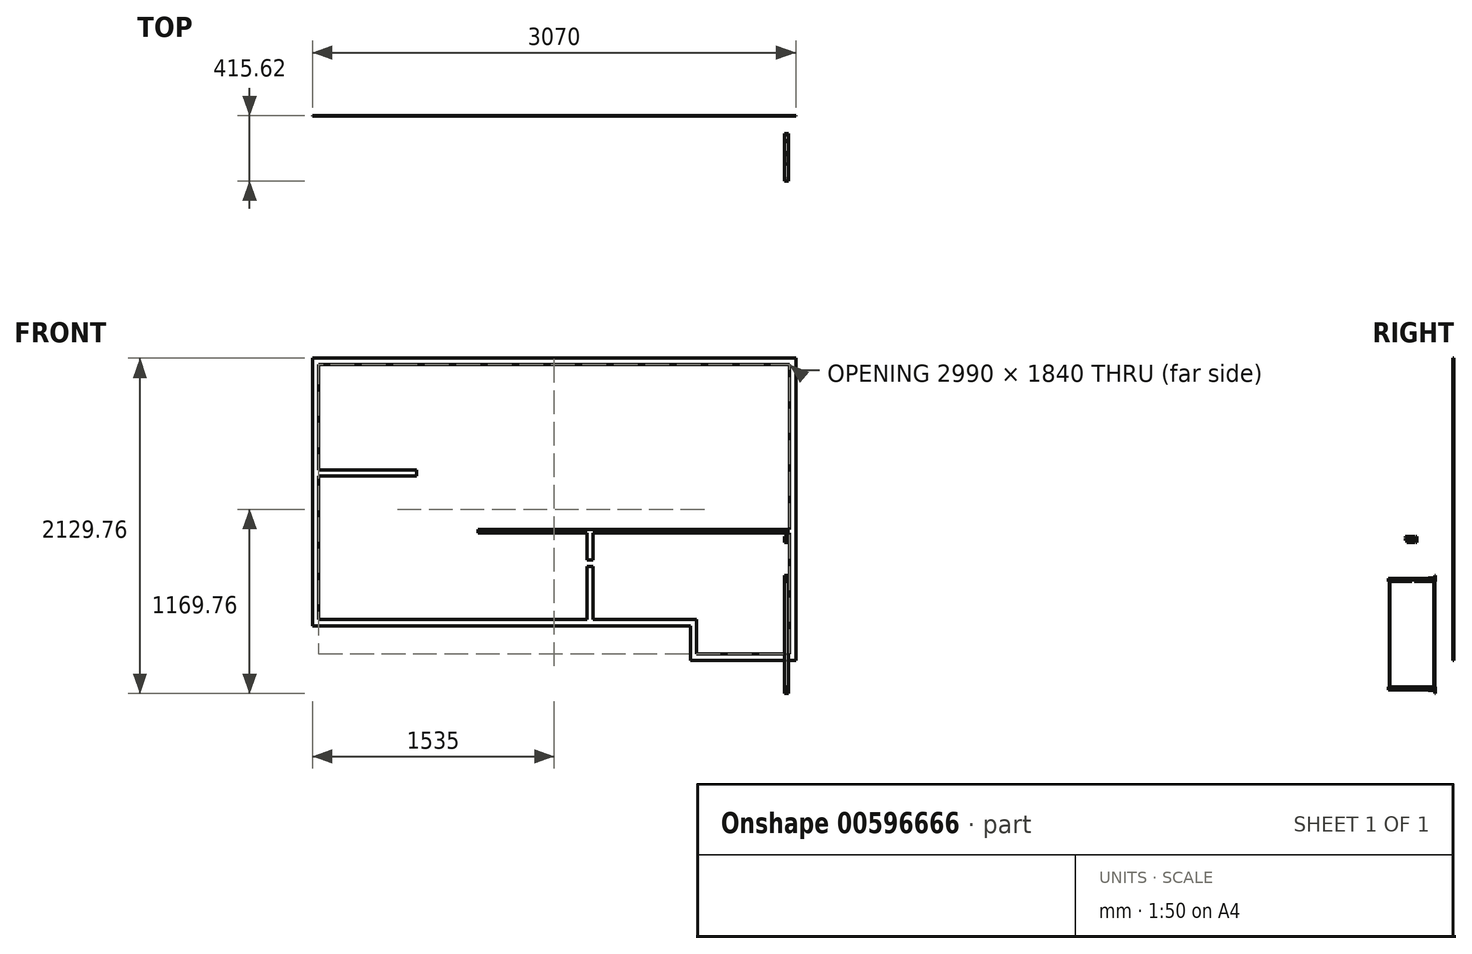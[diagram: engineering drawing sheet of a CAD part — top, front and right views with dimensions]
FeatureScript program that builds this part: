
annotation { "Feature Type Name" : "Feature", "Feature Type Description" : "" }
export const myFeature = defineFeature(function(context is Context, id is Id, definition is map)
    precondition{}
    {
        {
            var Q0;
            Q0=qCreatedBy(makeId("Front.planeOp"),FACE);
            var sketch = newSketch(context, id + "F0", { "sketchPlane" : qUnion([Q0])});
            skLineSegment(sketch, "E0.bottom", {"start": v(-2999.25, 2139.45) * mm, "end": v(70.75, 2139.45) * mm});
            skLineSegment(sketch, "E0.top", {"start": v(-599.25, 219.45) * mm, "end": v(70.75, 219.45) * mm});
            skLineSegment(sketch, "E0.left", {"start": v(-2999.25, 2139.45) * mm, "end": v(-2999.25, 439.45) * mm});
            skLineSegment(sketch, "E0.right", {"start": v(70.75, 2139.45) * mm, "end": v(70.75, 219.45) * mm});
            skLineSegment(sketch, "E1", {"start": v(-2999.25, 439.45) * mm, "end": v(-599.25, 439.45) * mm});
            skLineSegment(sketch, "E2", {"start": v(-599.25, 439.45) * mm, "end": v(-599.25, 219.45) * mm});
            skLineSegment(sketch, "E3.0", {"start": v(-2959.25, 2099.45) * mm, "end": v(-2959.25, 479.45) * mm});
            skLineSegment(sketch, "E3.1", {"start": v(30.75, 2099.45) * mm, "end": v(30.75, 1079.45) * mm});
            skLineSegment(sketch, "E3.2", {"start": v(-559.25, 259.45) * mm, "end": v(30.75, 259.45) * mm});
            skLineSegment(sketch, "E3.3", {"start": v(-2959.25, 2099.45) * mm, "end": v(30.75, 2099.45) * mm});
            skLineSegment(sketch, "E3.4", {"start": v(-559.25, 479.45) * mm, "end": v(-559.25, 259.45) * mm});
            skLineSegment(sketch, "E3.5", {"start": v(-2959.25, 479.45) * mm, "end": v(-559.25, 479.45) * mm});
            skLineSegment(sketch, "E4.top", {"start": v(-2959.25, 1029.45) * mm, "end": v(-1989.25, 1029.45) * mm});
            skLineSegment(sketch, "E4.left", {"start": v(-2959.25, 1069.45) * mm, "end": v(-2959.25, 1029.45) * mm});
            skLineSegment(sketch, "E4.right", {"start": v(30.75, 1079.45) * mm, "end": v(30.75, 1029.45) * mm});
            skLineSegment(sketch, "E5.bottom", {"start": v(-2339.25, 2099.45) * mm, "end": v(-2299.25, 2099.45) * mm});
            skLineSegment(sketch, "E5.top", {"start": v(-2339.25, 1069.45) * mm, "end": v(-2299.25, 1069.45) * mm});
            skLineSegment(sketch, "E5.left", {"start": v(-2339.25, 2099.45) * mm, "end": v(-2339.25, 1429.45) * mm});
            skLineSegment(sketch, "E5.right", {"start": v(-2299.25, 2099.45) * mm, "end": v(-2299.25, 1429.45) * mm});
            skLineSegment(sketch, "E6.bottom", {"start": v(-1989.25, 2099.45) * mm, "end": v(-1949.25, 2099.45) * mm});
            skLineSegment(sketch, "E6.left", {"start": v(-1989.25, 2099.45) * mm, "end": v(-1989.25, 1069.45) * mm});
            skLineSegment(sketch, "E6.right", {"start": v(-1949.25, 2099.45) * mm, "end": v(-1949.25, 1079.45) * mm});
            skLineSegment(sketch, "E7.bottom", {"start": v(-2959.25, 1429.45) * mm, "end": v(-2339.25, 1429.45) * mm});
            skLineSegment(sketch, "E7.top", {"start": v(-2959.25, 1389.45) * mm, "end": v(-2339.25, 1389.45) * mm});
            skLineSegment(sketch, "E7.left", {"start": v(-2959.25, 1429.45) * mm, "end": v(-2959.25, 1389.45) * mm});
            skLineSegment(sketch, "E7.right", {"start": v(-1989.25, 1429.45) * mm, "end": v(-1989.25, 1389.45) * mm});
            skLineSegment(sketch, "E8.bottom", {"start": v(-2649.25, 1029.45) * mm, "end": v(-2609.25, 1029.45) * mm});
            skLineSegment(sketch, "E8.top", {"start": v(-2649.25, 479.45) * mm, "end": v(-2609.25, 479.45) * mm});
            skLineSegment(sketch, "E8.left", {"start": v(-2649.25, 1029.45) * mm, "end": v(-2649.25, 479.45) * mm});
            skLineSegment(sketch, "E8.right", {"start": v(-2609.25, 1029.45) * mm, "end": v(-2609.25, 479.45) * mm});
            skLineSegment(sketch, "E9.bottom", {"start": v(-2609.25, 816.45) * mm, "end": v(-1256.25, 816.45) * mm});
            skLineSegment(sketch, "E9.top", {"start": v(-2609.25, 856.45) * mm, "end": v(-1949.25, 856.45) * mm});
            skLineSegment(sketch, "E9.left", {"start": v(-2609.25, 816.45) * mm, "end": v(-2609.25, 856.45) * mm});
            skLineSegment(sketch, "E9.right", {"start": v(30.75, 816.45) * mm, "end": v(30.75, 856.45) * mm});
            skLineSegment(sketch, "E10.bottom", {"start": v(-559.25, 479.45) * mm, "end": v(-599.25, 479.45) * mm});
            skLineSegment(sketch, "E10.top", {"start": v(-559.25, 816.45) * mm, "end": v(-599.25, 816.45) * mm});
            skLineSegment(sketch, "E10.left", {"start": v(-559.25, 479.45) * mm, "end": v(-559.25, 816.45) * mm});
            skLineSegment(sketch, "E10.right", {"start": v(-599.25, 479.45) * mm, "end": v(-599.25, 816.45) * mm});
            skLineSegment(sketch, "E11.top", {"start": v(-1989.25, 479.45) * mm, "end": v(-1949.25, 479.45) * mm});
            skLineSegment(sketch, "E11.left", {"start": v(-1989.25, 1069.45) * mm, "end": v(-1989.25, 856.45) * mm});
            skLineSegment(sketch, "E11.right", {"start": v(-1949.25, 1079.45) * mm, "end": v(-1949.25, 1079.45) * mm});
            skLineSegment(sketch, "E12", {"start": v(-1256.25, 479.45) * mm, "end": v(-1256.25, 816.45) * mm});
            skLineSegment(sketch, "E13", {"start": v(-1216.25, 1029.45) * mm, "end": v(-1216.25, 856.45) * mm});
            skLineSegment(sketch, "E14", {"start": v(-1949.25, 1049.45) * mm, "end": v(30.75, 1049.45) * mm});
            skPoint(sketch, "E14.endSnap0", {"position": v(30.75, 1054.45) * mm});
            skLineSegment(sketch, "E15", {"start": v(-1949.25, 1079.45) * mm, "end": v(-1949.25, 856.45) * mm});
            skLineSegment(sketch, "E16", {"start": v(30.75, 1079.45) * mm, "end": v(30.75, 259.45) * mm});
            skLineSegment(sketch, "E17", {"start": v(-1989.25, 1069.45) * mm, "end": v(-2959.25, 1069.45) * mm});
            skLineSegment(sketch, "E18", {"start": v(-1949.25, 1029.45) * mm, "end": v(30.75, 1029.45) * mm});
            skLineSegment(sketch, "E19", {"start": v(-2959.25, 479.45) * mm, "end": v(-2999.25, 439.45) * mm});
            skLineSegment(sketch, "E20", {"start": v(-2959.25, 2099.45) * mm, "end": v(-2999.25, 2139.45) * mm});
            skLineSegment(sketch, "E21", {"start": v(30.75, 2099.45) * mm, "end": v(70.75, 2139.45) * mm});
            skLineSegment(sketch, "E22", {"start": v(30.75, 259.45) * mm, "end": v(70.75, 219.45) * mm});
            skLineSegment(sketch, "E23", {"start": v(-559.25, 259.45) * mm, "end": v(-599.25, 219.45) * mm});
            skLineSegment(sketch, "E24", {"start": v(-559.25, 479.45) * mm, "end": v(-599.25, 439.45) * mm});
            skLineSegment(sketch, "E25", {"start": v(-1949.25, 856.45) * mm, "end": v(-1256.25, 856.45) * mm});
            skLineSegment(sketch, "E26", {"start": v(-1949.25, 816.45) * mm, "end": v(-1949.25, 479.45) * mm});
            skLineSegment(sketch, "E27", {"start": v(-1989.25, 816.45) * mm, "end": v(-1989.25, 479.45) * mm});
            skLineSegment(sketch, "E28", {"start": v(-1256.25, 856.45) * mm, "end": v(-1216.25, 856.45) * mm});
            skLineSegment(sketch, "E29", {"start": v(-1216.25, 816.45) * mm, "end": v(30.75, 816.45) * mm});
            skLineSegment(sketch, "E30", {"start": v(-1256.25, 856.45) * mm, "end": v(-1256.25, 1029.45) * mm});
            skLineSegment(sketch, "E31", {"start": v(-1216.25, 856.45) * mm, "end": v(30.75, 856.45) * mm});
            skLineSegment(sketch, "E32", {"start": v(-1216.25, 816.45) * mm, "end": v(-1216.25, 479.45) * mm});
            skLineSegment(sketch, "E33", {"start": v(-1256.25, 816.45) * mm, "end": v(-1216.25, 816.45) * mm});
            skLineSegment(sketch, "E34", {"start": v(-2339.25, 1429.45) * mm, "end": v(-2339.25, 1429.45) * mm});
            skLineSegment(sketch, "E35", {"start": v(-2339.25, 1389.45) * mm, "end": v(-2339.25, 1389.45) * mm});
            skLineSegment(sketch, "E36", {"start": v(-2299.25, 1389.45) * mm, "end": v(-2299.25, 1389.45) * mm});
            skLineSegment(sketch, "E37", {"start": v(-2299.25, 1429.45) * mm, "end": v(-2299.25, 1429.45) * mm});
            skLineSegment(sketch, "E38", {"start": v(-2339.25, 1389.45) * mm, "end": v(-2339.25, 1069.45) * mm});
            skLineSegment(sketch, "E39", {"start": v(-2339.25, 1429.45) * mm, "end": v(-2339.25, 1389.45) * mm});
            skLineSegment(sketch, "E40", {"start": v(-2299.25, 1429.45) * mm, "end": v(-2299.25, 1389.45) * mm});
            skLineSegment(sketch, "E41", {"start": v(-2299.25, 1389.45) * mm, "end": v(-2299.25, 1069.45) * mm});
            skLineSegment(sketch, "E42", {"start": v(-2299.25, 1429.45) * mm, "end": v(-1989.25, 1429.45) * mm});
            skLineSegment(sketch, "E43", {"start": v(-2299.25, 1389.45) * mm, "end": v(-1989.25, 1389.45) * mm});
            skSolve(sketch);
        }
        {
            var Q0;
            Q0 = qSketchRegion(id + "F0", true);
            var Q1;
            Q1=makeQuery(id+"F0.imprint","IMPRINT",FACE,{"disambiguationData":[TD([[makeQuery(id+"F0.imprint","IMPRINT",EDGE,{"derivedFrom":sQuery(id+"F0.wireOp",EDGE,"E7.bottom")}),-1.0]])]});
            var Q2;
            Q2=makeQuery(id+"F0.imprint","IMPRINT",FACE,{"disambiguationData":[TD([[makeQuery(id+"F0.imprint","IMPRINT",EDGE,{"derivedFrom":sQuery(id+"F0.wireOp",EDGE,"E5.bottom")}),-1.0]])]});
            var Q3;
            Q3=makeQuery(id+"F0.imprint","IMPRINT",FACE,{"disambiguationData":[TD([[makeQuery(id+"F0.imprint","IMPRINT",EDGE,{"derivedFrom":sQuery(id+"F0.wireOp",EDGE,"E7.right")}),-1.0]])]});
            var Q4;
            {var subQ9=sQuery(id+"F0.wireOp",EDGE,"E6.bottom");Q4=makeQuery(id+"F0.imprint","IMPRINT",FACE,{"disambiguationData":[TD([[makeQuery(id+"F0.imprint","IMPRINT",EDGE,{"derivedFrom":subQ9}),-1.0]])]});}
            var Q5;
            {var subQ1=sQuery(id+"F0.wireOp",EDGE,"E4.left");Q5=makeQuery(id+"F0.imprint","IMPRINT",FACE,{"disambiguationData":[TD([[makeQuery(id+"F0.imprint","IMPRINT",EDGE,{"derivedFrom":subQ1}),1.0]])]});}
            var Q6;
            {var subQ1=sQuery(id+"F0.wireOp",EDGE,"E8.bottom");Q6=makeQuery(id+"F0.imprint","IMPRINT",FACE,{"disambiguationData":[TD([[makeQuery(id+"F0.imprint","IMPRINT",EDGE,{"derivedFrom":subQ1}),-1.0]])]});}
            var Q7;
            {var subQ6=sQuery(id+"F0.wireOp",EDGE,"E9.left");Q7=makeQuery(id+"F0.imprint","IMPRINT",FACE,{"disambiguationData":[TD([[makeQuery(id+"F0.imprint","IMPRINT",EDGE,{"derivedFrom":subQ6}),-1.0]])]});}
            var Q8;
            Q8=makeQuery(id+"F0.imprint","IMPRINT",FACE,{"disambiguationData":[TD([[makeQuery(id+"F0.imprint","IMPRINT",EDGE,{"derivedFrom":sQuery(id+"F0.wireOp",EDGE,"E11.top")}),1.0]])]});
            var Q9;
            {var subQ4=sQuery(id+"F0.wireOp",EDGE,"E14");Q9=makeQuery(id+"F0.imprint","IMPRINT",FACE,{"disambiguationData":[TD([[makeQuery(id+"F0.imprint","IMPRINT",EDGE,{"derivedFrom":subQ4}),-1.0]])]});}
            var Q10;
            {var subQ0=sQuery(id+"F0.wireOp",EDGE,"E13");Q10=makeQuery(id+"F0.imprint","IMPRINT",FACE,{"disambiguationData":[TD([[makeQuery(id+"F0.imprint","IMPRINT",EDGE,{"derivedFrom":subQ0}),-1.0]])]});}
            var Q11;
            {var subQ0=sQuery(id+"F0.wireOp",EDGE,"E12");Q11=makeQuery(id+"F0.imprint","IMPRINT",FACE,{"disambiguationData":[TD([[makeQuery(id+"F0.imprint","IMPRINT",EDGE,{"derivedFrom":subQ0}),-1.0]])]});}
            var Q12;
            Q12=makeQuery(id+"F0.imprint","IMPRINT",FACE,{"disambiguationData":[TD([[makeQuery(id+"F0.imprint","IMPRINT",EDGE,{"derivedFrom":sQuery(id+"F0.wireOp",EDGE,"E10.bottom")}),-1.0]])]});
            extrude(context, id + "F1", {"entities" : qUnion([Q0, Q1, Q2, Q3, Q4, Q5, Q6, Q7, Q8, Q9, Q10, Q11, Q12]), "depth" : 5 * mm, "offsetDistance" : 25 * mm});
        }
        {
            var Q0;
            Q0=qCreatedBy(makeId("Right.planeOp"),FACE);
            var sketch = newSketch(context, id + "F2", { "sketchPlane" : qUnion([Q0])});
            skLineSegment(sketch, "E44.bottom", {"start": v(-115.62, 49.7) * mm, "end": v(-120.62, 49.7) * mm});
            skLineSegment(sketch, "E44.top", {"start": v(-115.62, 9.7) * mm, "end": v(-120.62, 9.7) * mm});
            skLineSegment(sketch, "E44.left", {"start": v(-115.62, 49.7) * mm, "end": v(-115.62, 9.7) * mm});
            skLineSegment(sketch, "E44.right", {"start": v(-120.62, 49.7) * mm, "end": v(-120.62, 32.2) * mm});
            skLineSegment(sketch, "E45.bottom", {"start": v(-120.62, 27.2) * mm, "end": v(-160.62, 27.2) * mm});
            skLineSegment(sketch, "E45.top", {"start": v(-120.62, 32.2) * mm, "end": v(-160.62, 32.2) * mm});
            skLineSegment(sketch, "E45.right", {"start": v(-160.62, 32.2) * mm, "end": v(-160.62, 27.2) * mm});
            skLineSegment(sketch, "E46.bottom", {"start": v(-115.62, 759.7) * mm, "end": v(-120.62, 759.7) * mm});
            skLineSegment(sketch, "E46.top", {"start": v(-115.62, 719.7) * mm, "end": v(-120.62, 719.7) * mm});
            skLineSegment(sketch, "E46.left", {"start": v(-115.62, 759.7) * mm, "end": v(-115.62, 719.7) * mm});
            skLineSegment(sketch, "E46.right", {"start": v(-120.62, 759.7) * mm, "end": v(-120.62, 742.2) * mm});
            skLineSegment(sketch, "E47.bottom", {"start": v(-120.62, 742.2) * mm, "end": v(-160.62, 742.2) * mm});
            skLineSegment(sketch, "E47.top", {"start": v(-120.62, 737.2) * mm, "end": v(-160.62, 737.2) * mm});
            skLineSegment(sketch, "E47.right", {"start": v(-160.62, 737.2) * mm, "end": v(-160.62, 742.2) * mm});
            skLineSegment(sketch, "E48", {"start": v(-120.62, 737.2) * mm, "end": v(-120.62, 719.7) * mm});
            skLineSegment(sketch, "E49", {"start": v(-120.62, 27.2) * mm, "end": v(-120.62, 9.7) * mm});
            skLineSegment(sketch, "E50.bottom", {"start": v(-121.62, 735.2) * mm, "end": v(-127.62, 735.2) * mm});
            skLineSegment(sketch, "E50.top", {"start": v(-121.62, 34.2) * mm, "end": v(-127.62, 34.2) * mm});
            skLineSegment(sketch, "E50.left", {"start": v(-121.62, 735.2) * mm, "end": v(-121.62, 34.2) * mm});
            skLineSegment(sketch, "E50.right", {"start": v(-127.62, 735.2) * mm, "end": v(-127.62, 34.2) * mm});
            skLineSegment(sketch, "E51.bottom", {"start": v(-164.62, 738.94) * mm, "end": v(-415.62, 738.94) * mm});
            skLineSegment(sketch, "E51.left", {"start": v(-164.62, 738.94) * mm, "end": v(-164.62, 735.2) * mm});
            skLineSegment(sketch, "E51.right", {"start": v(-415.62, 738.94) * mm, "end": v(-415.62, 720.2) * mm});
            skLineSegment(sketch, "E52.bottom", {"start": v(-415.62, 720.2) * mm, "end": v(-409.62, 720.2) * mm});
            skLineSegment(sketch, "E52.top", {"start": v(-164.62, 735.2) * mm, "end": v(-129.62, 735.2) * mm});
            skLineSegment(sketch, "E52.right", {"start": v(-129.62, 720.2) * mm, "end": v(-129.62, 735.2) * mm});
            skLineSegment(sketch, "E53", {"start": v(-129.62, 34.2) * mm, "end": v(-129.62, 49.2) * mm});
            skLineSegment(sketch, "E54", {"start": v(-129.62, 49.2) * mm, "end": v(-398.62, 49.2) * mm});
            skLineSegment(sketch, "E55", {"start": v(-415.62, 49.2) * mm, "end": v(-415.62, 31.2) * mm});
            skLineSegment(sketch, "E56", {"start": v(-415.62, 31.2) * mm, "end": v(-164.62, 31.2) * mm});
            skLineSegment(sketch, "E57", {"start": v(-164.62, 31.2) * mm, "end": v(-164.62, 34.2) * mm});
            skLineSegment(sketch, "E58", {"start": v(-164.62, 34.2) * mm, "end": v(-129.62, 34.2) * mm});
            skLineSegment(sketch, "E59.top", {"start": v(-409.62, 44.2) * mm, "end": v(-406.62, 44.2) * mm});
            skLineSegment(sketch, "E59.left", {"start": v(-409.62, 49.2) * mm, "end": v(-409.62, 44.2) * mm});
            skLineSegment(sketch, "E59.right", {"start": v(-406.62, 49.2) * mm, "end": v(-406.62, 44.2) * mm});
            skLineSegment(sketch, "E60", {"start": v(-409.62, 49.2) * mm, "end": v(-415.62, 49.2) * mm});
            skLineSegment(sketch, "E61.top", {"start": v(-409.62, 728.94) * mm, "end": v(-406.62, 728.94) * mm});
            skLineSegment(sketch, "E61.left", {"start": v(-409.62, 720.2) * mm, "end": v(-409.62, 728.94) * mm});
            skLineSegment(sketch, "E61.right", {"start": v(-406.62, 720.2) * mm, "end": v(-406.62, 728.94) * mm});
            skLineSegment(sketch, "E62", {"start": v(-406.62, 720.94) * mm, "end": v(-401.62, 720.94) * mm});
            skLineSegment(sketch, "E63.bottom", {"start": v(-409.35, 44.2) * mm, "end": v(-406.99, 44.2) * mm});
            skLineSegment(sketch, "E63.top", {"start": v(-409.35, 722.2) * mm, "end": v(-406.99, 722.2) * mm});
            skLineSegment(sketch, "E63.left", {"start": v(-409.35, 44.2) * mm, "end": v(-409.35, 722.2) * mm});
            skLineSegment(sketch, "E63.right", {"start": v(-406.99, 44.2) * mm, "end": v(-406.99, 722.2) * mm});
            skLineSegment(sketch, "E64.top", {"start": v(-265.62, 731.2) * mm, "end": v(-249.62, 731.2) * mm});
            skLineSegment(sketch, "E64.left", {"start": v(-265.62, 720.94) * mm, "end": v(-265.62, 731.2) * mm});
            skLineSegment(sketch, "E64.right", {"start": v(-249.62, 720.2) * mm, "end": v(-249.62, 731.2) * mm});
            skLineSegment(sketch, "E65", {"start": v(-249.62, 720.2) * mm, "end": v(-129.62, 720.2) * mm});
            skLineSegment(sketch, "E66.top", {"start": v(-401.62, 728.94) * mm, "end": v(-398.62, 728.94) * mm});
            skLineSegment(sketch, "E66.left", {"start": v(-401.62, 720.94) * mm, "end": v(-401.62, 728.94) * mm});
            skLineSegment(sketch, "E66.right", {"start": v(-398.62, 720.94) * mm, "end": v(-398.62, 728.94) * mm});
            skLineSegment(sketch, "E67", {"start": v(-398.62, 720.94) * mm, "end": v(-265.62, 720.94) * mm});
            skLineSegment(sketch, "E68.top", {"start": v(-401.62, 44.2) * mm, "end": v(-398.62, 44.2) * mm});
            skLineSegment(sketch, "E68.left", {"start": v(-401.62, 49.2) * mm, "end": v(-401.62, 44.2) * mm});
            skLineSegment(sketch, "E68.right", {"start": v(-398.62, 49.2) * mm, "end": v(-398.62, 44.2) * mm});
            skLineSegment(sketch, "E69", {"start": v(-401.62, 49.2) * mm, "end": v(-406.62, 49.2) * mm});
            skSolve(sketch);
        }
        {
            var Q0;
            Q0 = qSketchRegion(id + "F2", true);
            extrude(context, id + "F3", {"entities" : qUnion([Q0]), "depth" : 25 * mm, "offsetDistance" : 25 * mm});
        }
        {
            var Q0;
            Q0=qCreatedBy(makeId("Right.planeOp"),FACE);
            var sketch = newSketch(context, id + "F4", { "sketchPlane" : qUnion([Q0])});
            skLineSegment(sketch, "E70.bottom", {"start": v(-279.42, 990.24) * mm, "end": v(-239.42, 990.24) * mm});
            skLineSegment(sketch, "E70.top", {"start": v(-279.42, 985.24) * mm, "end": v(-239.42, 985.24) * mm});
            skLineSegment(sketch, "E70.left", {"start": v(-279.42, 990.24) * mm, "end": v(-279.42, 985.24) * mm});
            skLineSegment(sketch, "E71.bottom", {"start": v(-239.42, 967.74) * mm, "end": v(-234.42, 967.74) * mm});
            skLineSegment(sketch, "E71.top", {"start": v(-239.42, 1007.74) * mm, "end": v(-234.42, 1007.74) * mm});
            skLineSegment(sketch, "E71.left", {"start": v(-239.42, 967.74) * mm, "end": v(-239.42, 985.24) * mm});
            skLineSegment(sketch, "E71.right", {"start": v(-234.42, 967.74) * mm, "end": v(-234.42, 1007.74) * mm});
            skLineSegment(sketch, "E72.trimOffspring", {"start": v(-239.42, 990.24) * mm, "end": v(-239.42, 1007.74) * mm});
            skLineSegment(sketch, "E73.bottom", {"start": v(-308.42, 1005.74) * mm, "end": v(-248.42, 1005.74) * mm});
            skLineSegment(sketch, "E73.right", {"start": v(-248.42, 1005.74) * mm, "end": v(-248.42, 991.74) * mm});
            skLineSegment(sketch, "E74", {"start": v(-281.42, 991.74) * mm, "end": v(-248.42, 991.74) * mm});
            skLineSegment(sketch, "E75.MirrorCS", {"start": v(-308.42, 981.74) * mm, "end": v(-308.42, 987.74) * mm});
            skLineSegment(sketch, "E76.MirrorCS", {"start": v(-248.42, 969.74) * mm, "end": v(-248.42, 983.74) * mm});
            skLineSegment(sketch, "E77.MirrorCS", {"start": v(-281.42, 983.74) * mm, "end": v(-248.42, 983.74) * mm});
            skLineSegment(sketch, "E78", {"start": v(-308.42, 981.74) * mm, "end": v(-296.42, 981.74) * mm});
            skLineSegment(sketch, "E79", {"start": v(-296.42, 981.74) * mm, "end": v(-296.42, 969.74) * mm});
            skLineSegment(sketch, "E80", {"start": v(-308.42, 1005.74) * mm, "end": v(-308.42, 1000.74) * mm});
            skLineSegment(sketch, "E81", {"start": v(-248.42, 969.74) * mm, "end": v(-296.42, 969.74) * mm});
            skLineSegment(sketch, "E82", {"start": v(-281.42, 983.74) * mm, "end": v(-281.42, 987.74) * mm});
            skLineSegment(sketch, "E83", {"start": v(-281.42, 987.74) * mm, "end": v(-308.42, 987.74) * mm});
            skLineSegment(sketch, "E84", {"start": v(-281.42, 987.74) * mm, "end": v(-281.42, 991.74) * mm});
            skLineSegment(sketch, "E85", {"start": v(-308.42, 993.74) * mm, "end": v(-296.42, 993.74) * mm});
            skLineSegment(sketch, "E86", {"start": v(-296.42, 993.74) * mm, "end": v(-296.42, 1000.74) * mm});
            skLineSegment(sketch, "E87", {"start": v(-296.42, 1000.74) * mm, "end": v(-308.42, 1000.74) * mm});
            skLineSegment(sketch, "E88.trimOffspring", {"start": v(-308.42, 993.74) * mm, "end": v(-308.42, 987.74) * mm});
            skSolve(sketch);
        }
        {
            var Q0;
            Q0=makeQuery(id+"F4.imprint","IMPRINT",FACE,{"disambiguationData":[TD([[makeQuery(id+"F4.imprint","IMPRINT",EDGE,{"derivedFrom":sQuery(id+"F4.wireOp",EDGE,"E70.bottom")}),-1.0]])]});
            var Q1;
            Q1=makeQuery(id+"F4.imprint","IMPRINT",FACE,{"disambiguationData":[TD([[makeQuery(id+"F4.imprint","IMPRINT",EDGE,{"derivedFrom":sQuery(id+"F4.wireOp",EDGE,"E73.bottom")}),-1.0]])]});
            extrude(context, id + "F5", {"entities" : qUnion([Q0, Q1]), "depth" : 25 * mm, "offsetDistance" : 25 * mm});
        }
        {
            var Q0;
            Q0=makeQuery(id+"F4.imprint","IMPRINT",FACE,{"disambiguationData":[TD([[makeQuery(id+"F4.imprint","IMPRINT",EDGE,{"derivedFrom":sQuery(id+"F4.wireOp",EDGE,"E75.MirrorCS")}),-1.0]])]});
            extrude(context, id + "F6", {"entities" : qUnion([Q0]), "depth" : 25 * mm, "offsetDistance" : 25 * mm});
        }
    });
